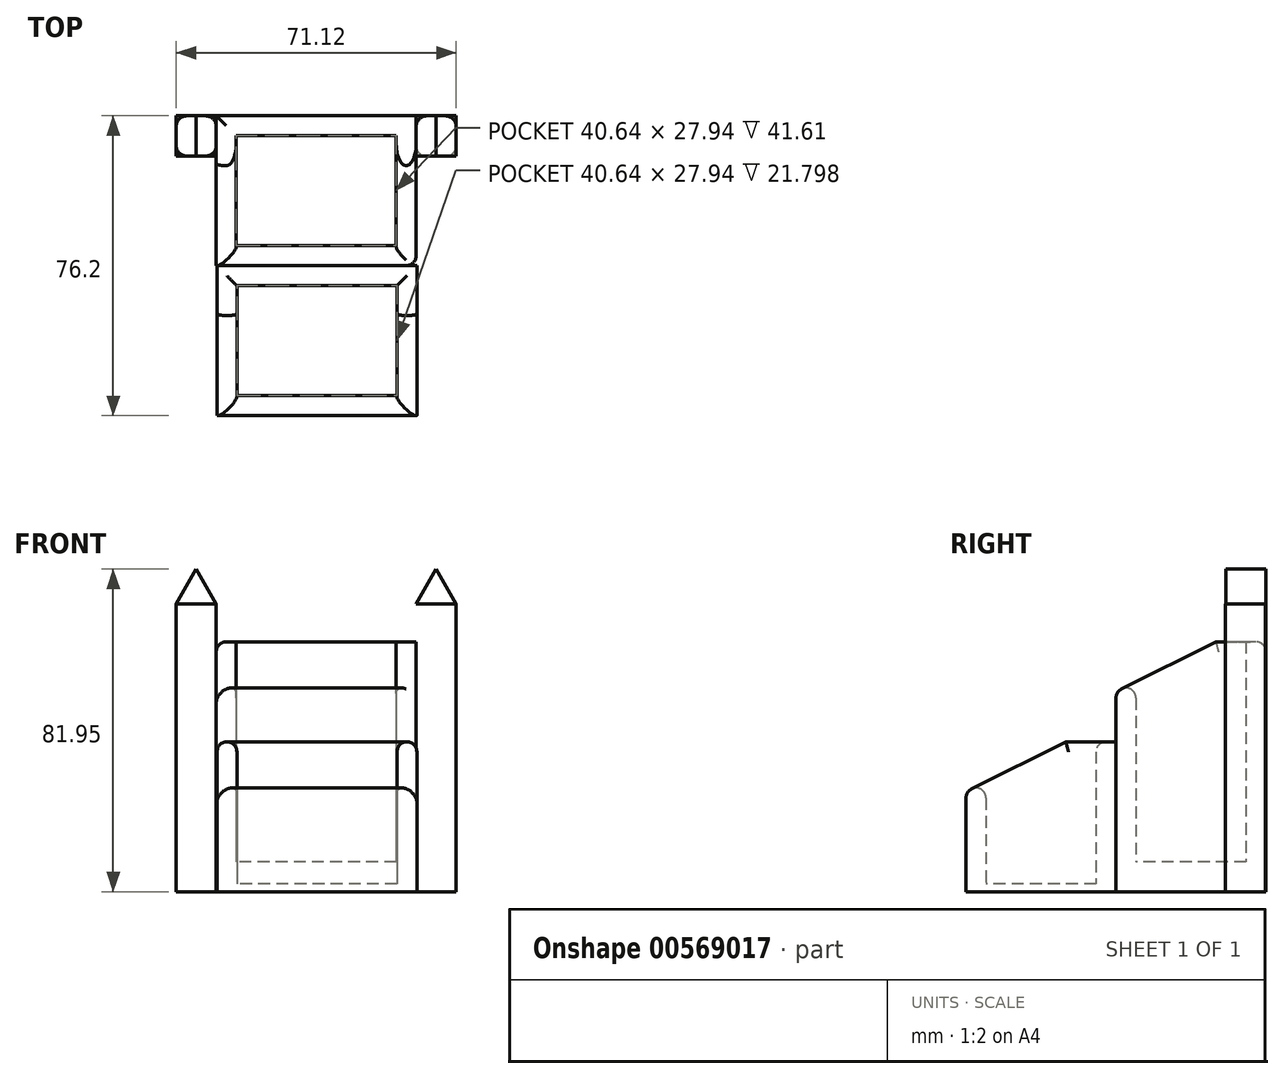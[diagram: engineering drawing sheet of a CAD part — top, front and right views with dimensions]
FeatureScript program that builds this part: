
annotation { "Feature Type Name" : "Feature", "Feature Type Description" : "" }
export const myFeature = defineFeature(function(context is Context, id is Id, definition is map)
    precondition{}
    {
        {
            var Q0;
            Q0=qCreatedBy(makeId("Top.planeOp"),FACE);
            var sketch = newSketch(context, id + "F0", { "sketchPlane" : qUnion([Q0])});
            skLineSegment(sketch, "E0", {"start": v(-32.91, 61.8) * mm, "end": v(-32.91, 23.7) * mm});
            skLineSegment(sketch, "E1", {"start": v(-32.91, 23.7) * mm, "end": v(17.89, 23.7) * mm});
            skLineSegment(sketch, "E2", {"start": v(17.89, 23.7) * mm, "end": v(17.89, 61.8) * mm});
            skLineSegment(sketch, "E3", {"start": v(17.89, 61.8) * mm, "end": v(-32.91, 61.8) * mm});
            skSolve(sketch);
        }
        {
            var Q0;
            Q0=qCreatedBy(makeId("Top.planeOp"),FACE);
            var sketch = newSketch(context, id + "F1", { "sketchPlane" : qUnion([Q0])});
            skLineSegment(sketch, "E4", {"start": v(-32.74, 23.7) * mm, "end": v(-32.74, -14.4) * mm});
            skLineSegment(sketch, "E5", {"start": v(-32.74, -14.4) * mm, "end": v(18.06, -14.4) * mm});
            skLineSegment(sketch, "E6", {"start": v(18.06, -14.4) * mm, "end": v(18.06, 23.7) * mm});
            skLineSegment(sketch, "E7", {"start": v(18.06, 23.7) * mm, "end": v(-32.74, 23.7) * mm});
            skSolve(sketch);
        }
        {
            var Q0;
            Q0=qCreatedBy(makeId("Top.planeOp"),FACE);
            var sketch = newSketch(context, id + "F2", { "sketchPlane" : qUnion([Q0])});
            skLineSegment(sketch, "E8", {"start": v(-27.83, 56.71) * mm, "end": v(-27.83, 28.77) * mm});
            skLineSegment(sketch, "E9", {"start": v(-27.83, 28.77) * mm, "end": v(12.8, 28.77) * mm});
            skLineSegment(sketch, "E10", {"start": v(12.8, 28.77) * mm, "end": v(12.8, 56.71) * mm});
            skLineSegment(sketch, "E11", {"start": v(12.8, 56.71) * mm, "end": v(-27.83, 56.71) * mm});
            skSolve(sketch);
        }
        {
            var Q0;
            Q0=qCreatedBy(makeId("Top.planeOp"),FACE);
            var sketch = newSketch(context, id + "F3", { "sketchPlane" : qUnion([Q0])});
            skLineSegment(sketch, "E12", {"start": v(-27.66, 18.61) * mm, "end": v(-27.66, -9.33) * mm});
            skLineSegment(sketch, "E13", {"start": v(-27.66, -9.33) * mm, "end": v(12.98, -9.33) * mm});
            skLineSegment(sketch, "E14", {"start": v(12.98, -9.33) * mm, "end": v(12.98, 18.61) * mm});
            skLineSegment(sketch, "E15", {"start": v(12.98, 18.61) * mm, "end": v(-27.66, 18.61) * mm});
            skSolve(sketch);
        }
        {
            var Q0;
            Q0 = qSketchRegion(id + "F0", true);
            extrude(context, id + "F4", {"entities" : qUnion([Q0]), "depth" : 63.5 * mm, "offsetDistance" : 25.4 * mm});
        }
        {
            var Q0;
            Q0 = qSketchRegion(id + "F1", true);
            extrude(context, id + "F5", {"entities" : qUnion([Q0]), "depth" : 38.1 * mm, "offsetDistance" : 25.4 * mm});
        }
        {
            var Q0;
            Q0 = qSketchRegion(id + "F2", true);
            extrude(context, id + "F6", {"entities" : qUnion([Q0]), "operationType" : NewBodyOperationType.REMOVE, "depth" : 63.5 * mm, "offsetDistance" : 25.4 * mm, "hasSecondDirection" : true, "secondDirectionOppositeDirection" : false, "secondDirectionDepth" : 7.62 * mm});
        }
        {
            var Q0;
            Q0 = qSketchRegion(id + "F3", true);
            extrude(context, id + "F7", {"entities" : qUnion([Q0]), "operationType" : NewBodyOperationType.REMOVE, "depth" : 61.2 * mm, "offsetDistance" : 25.4 * mm, "hasSecondDirection" : true, "secondDirectionOppositeDirection" : false, "secondDirectionDepth" : 2.03 * mm});
        }
        {
            var Q0;
            Q0=qCreatedBy(makeId("Top.planeOp"),FACE);
            var sketch = newSketch(context, id + "F8", { "sketchPlane" : qUnion([Q0])});
            skLineSegment(sketch, "E16", {"start": v(-32.91, 61.73) * mm, "end": v(-43.07, 61.73) * mm});
            skLineSegment(sketch, "E17", {"start": v(-43.07, 61.73) * mm, "end": v(-43.07, 51.57) * mm});
            skLineSegment(sketch, "E18", {"start": v(-43.07, 51.57) * mm, "end": v(-32.91, 51.57) * mm});
            skLineSegment(sketch, "E19", {"start": v(-32.91, 51.57) * mm, "end": v(-32.91, 61.73) * mm});
            skLineSegment(sketch, "E20", {"start": v(17.89, 61.7) * mm, "end": v(17.89, 51.54) * mm});
            skLineSegment(sketch, "E21", {"start": v(17.89, 51.54) * mm, "end": v(28.05, 51.54) * mm});
            skLineSegment(sketch, "E22", {"start": v(28.05, 51.54) * mm, "end": v(28.05, 61.7) * mm});
            skLineSegment(sketch, "E23", {"start": v(28.05, 61.7) * mm, "end": v(17.89, 61.7) * mm});
            skSolve(sketch);
        }
        {
            var Q0;
            Q0 = qSketchRegion(id + "F8", true);
            extrude(context, id + "F9", {"entities" : qUnion([Q0]), "depth" : 73.15 * mm, "offsetDistance" : 25.4 * mm});
        }
        {
            var Q0;
            Q0=qCreatedBy(makeId("Front.planeOp"),FACE);
            var sketch = newSketch(context, id + "F10", { "sketchPlane" : qUnion([Q0])});
            skLineSegment(sketch, "E24", {"start": v(-43.07, 73.15) * mm, "end": v(-32.91, 73.15) * mm});
            skLineSegment(sketch, "E25", {"start": v(-32.91, 73.15) * mm, "end": v(-38, 81.95) * mm});
            skLineSegment(sketch, "E26", {"start": v(-38, 81.95) * mm, "end": v(-43.07, 73.15) * mm});
            skLineSegment(sketch, "E27", {"start": v(17.89, 73.15) * mm, "end": v(28.05, 73.15) * mm});
            skLineSegment(sketch, "E28", {"start": v(28.05, 73.15) * mm, "end": v(22.97, 81.95) * mm});
            skLineSegment(sketch, "E29", {"start": v(22.97, 81.95) * mm, "end": v(17.89, 73.15) * mm});
            skSolve(sketch);
        }
        {
            var Q0;
            Q0 = qSketchRegion(id + "F10", true);
            extrude(context, id + "F11", {"entities" : qUnion([Q0]), "oppositeDirection" : true, "depth" : 61.77 * mm, "offsetDistance" : 25.4 * mm, "hasSecondDirection" : true, "secondDirectionOppositeDirection" : true, "secondDirectionDepth" : 51.56 * mm});
        }
        {
            var Q0;
            Q0=makeQuery(id+"F5.opExtrude","CAP_EDGE",EDGE,{"disambiguationData":[OSD([sQuery(id+"F1.wireOp",EDGE,"E5")])],"isStart":false});
            var Q1;
            Q1=makeQuery(id+"F4.opExtrude","CAP_EDGE",EDGE,{"disambiguationData":[OSD([sQuery(id+"F0.wireOp",EDGE,"E1")])],"isStart":false});
            chamfer(context, id + "F12", {"entities" : qUnion([Q0, Q1]), "chamferType" : ChamferType.TWO_OFFSETS, "width1" : 25.4 * mm, "oppositeDirection" : false, "width2" : 12.7 * mm, "tangentPropagation" : true});
        }
        {
            var Q0;
            Q0=makeQuery(id+"F7.boolean.opBoolean","INTERSECT",EDGE,{"derivedFrom":[makeQuery(id+"F5.opExtrude","CAP_FACE",FACE,{"disambiguationData":[OSD([sQuery(id+"F1.wireOp",EDGE,"E4"),sQuery(id+"F1.wireOp",EDGE,"E5"),sQuery(id+"F1.wireOp",EDGE,"E6"),sQuery(id+"F1.wireOp",EDGE,"E7")])],"isStart":false}),makeQuery(id+"F7.opExtrude","SWEPT_FACE",FACE,{"disambiguationData":[OSD([sQuery(id+"F3.wireOp",EDGE,"E15")])]})]});
            var Q1;
            Q1=makeQuery(id+"F7.boolean.opBoolean","INTERSECT",EDGE,{"derivedFrom":[makeQuery(id+"F5.opExtrude","CAP_FACE",FACE,{"disambiguationData":[OSD([sQuery(id+"F1.wireOp",EDGE,"E4"),sQuery(id+"F1.wireOp",EDGE,"E5"),sQuery(id+"F1.wireOp",EDGE,"E6"),sQuery(id+"F1.wireOp",EDGE,"E7")])],"isStart":false}),makeQuery(id+"F7.opExtrude","SWEPT_FACE",FACE,{"disambiguationData":[OSD([sQuery(id+"F3.wireOp",EDGE,"E12")])]})]});
            var Q2;
            Q2=makeQuery(id+"F12.opChamfer","BLEND_EDGE",EDGE,{"blendedFrom":[makeQuery(id+"F5.opExtrude","CAP_EDGE",EDGE,{"disambiguationData":[OSD([sQuery(id+"F1.wireOp",EDGE,"E5")])],"isStart":false}),makeQuery(id+"F7.boolean.opBoolean","COPY",FACE,{"derivedFrom":makeQuery(id+"F7.opExtrude","SWEPT_FACE",FACE,{"disambiguationData":[OSD([sQuery(id+"F3.wireOp",EDGE,"E12")])]})})],"blendedInto":[makeQuery(id+"F7.boolean.opBoolean","COPY",FACE,{"derivedFrom":makeQuery(id+"F7.opExtrude","SWEPT_FACE",FACE,{"disambiguationData":[OSD([sQuery(id+"F3.wireOp",EDGE,"E12")])]})})]});
            var Q3;
            Q3=makeQuery(id+"F12.opChamfer","BLEND_EDGE",EDGE,{"blendedFrom":[makeQuery(id+"F5.opExtrude","CAP_EDGE",EDGE,{"disambiguationData":[OSD([sQuery(id+"F1.wireOp",EDGE,"E5")])],"isStart":false}),makeQuery(id+"F7.boolean.opBoolean","COPY",FACE,{"derivedFrom":makeQuery(id+"F7.opExtrude","SWEPT_FACE",FACE,{"disambiguationData":[OSD([sQuery(id+"F3.wireOp",EDGE,"E14")])]})})],"blendedInto":[makeQuery(id+"F7.boolean.opBoolean","COPY",FACE,{"derivedFrom":makeQuery(id+"F7.opExtrude","SWEPT_FACE",FACE,{"disambiguationData":[OSD([sQuery(id+"F3.wireOp",EDGE,"E14")])]})})]});
            var Q4;
            Q4=makeQuery(id+"F7.boolean.opBoolean","INTERSECT",EDGE,{"derivedFrom":[makeQuery(id+"F5.opExtrude","CAP_FACE",FACE,{"disambiguationData":[OSD([sQuery(id+"F1.wireOp",EDGE,"E4"),sQuery(id+"F1.wireOp",EDGE,"E5"),sQuery(id+"F1.wireOp",EDGE,"E6"),sQuery(id+"F1.wireOp",EDGE,"E7")])],"isStart":false}),makeQuery(id+"F7.opExtrude","SWEPT_FACE",FACE,{"disambiguationData":[OSD([sQuery(id+"F3.wireOp",EDGE,"E14")])]})]});
            var Q5;
            Q5=makeQuery(id+"F12.opChamfer","BLEND_EDGE",EDGE,{"blendedFrom":[makeQuery(id+"F5.opExtrude","CAP_EDGE",EDGE,{"disambiguationData":[OSD([sQuery(id+"F1.wireOp",EDGE,"E5")])],"isStart":false}),makeQuery(id+"F7.boolean.opBoolean","COPY",FACE,{"derivedFrom":makeQuery(id+"F7.opExtrude","SWEPT_FACE",FACE,{"disambiguationData":[OSD([sQuery(id+"F3.wireOp",EDGE,"E13")])]})})],"blendedInto":[makeQuery(id+"F7.boolean.opBoolean","COPY",FACE,{"derivedFrom":makeQuery(id+"F7.opExtrude","SWEPT_FACE",FACE,{"disambiguationData":[OSD([sQuery(id+"F3.wireOp",EDGE,"E13")])]})})]});
            var Q6;
            Q6=makeQuery(id+"F12.opChamfer","BLEND_EDGE",EDGE,{"blendedFrom":[makeQuery(id+"F4.opExtrude","CAP_EDGE",EDGE,{"disambiguationData":[OSD([sQuery(id+"F0.wireOp",EDGE,"E1")])],"isStart":false}),makeQuery(id+"F6.boolean.opBoolean","COPY",FACE,{"derivedFrom":makeQuery(id+"F6.opExtrude","SWEPT_FACE",FACE,{"disambiguationData":[OSD([sQuery(id+"F2.wireOp",EDGE,"E9")])]})})],"blendedInto":[makeQuery(id+"F6.boolean.opBoolean","COPY",FACE,{"derivedFrom":makeQuery(id+"F6.opExtrude","SWEPT_FACE",FACE,{"disambiguationData":[OSD([sQuery(id+"F2.wireOp",EDGE,"E9")])]})})]});
            var Q7;
            Q7=makeQuery(id+"F12.opChamfer","BLEND_EDGE",EDGE,{"blendedFrom":[makeQuery(id+"F4.opExtrude","CAP_EDGE",EDGE,{"disambiguationData":[OSD([sQuery(id+"F0.wireOp",EDGE,"E1")])],"isStart":false}),makeQuery(id+"F6.boolean.opBoolean","COPY",FACE,{"derivedFrom":makeQuery(id+"F6.opExtrude","SWEPT_FACE",FACE,{"disambiguationData":[OSD([sQuery(id+"F2.wireOp",EDGE,"E8")])]})})],"blendedInto":[makeQuery(id+"F6.boolean.opBoolean","COPY",FACE,{"derivedFrom":makeQuery(id+"F6.opExtrude","SWEPT_FACE",FACE,{"disambiguationData":[OSD([sQuery(id+"F2.wireOp",EDGE,"E8")])]})})]});
            var Q8;
            Q8=makeQuery(id+"F6.boolean.opBoolean","COPY",EDGE,{"derivedFrom":makeQuery(id+"F6.opExtrude","CAP_EDGE",EDGE,{"disambiguationData":[OSD([sQuery(id+"F2.wireOp",EDGE,"E8")])],"isStart":false})});
            var Q9;
            Q9=makeQuery(id+"F6.boolean.opBoolean","COPY",EDGE,{"derivedFrom":makeQuery(id+"F6.opExtrude","CAP_EDGE",EDGE,{"disambiguationData":[OSD([sQuery(id+"F2.wireOp",EDGE,"E11")])],"isStart":false})});
            var Q10;
            Q10=makeQuery(id+"F6.boolean.opBoolean","COPY",EDGE,{"derivedFrom":makeQuery(id+"F6.opExtrude","CAP_EDGE",EDGE,{"disambiguationData":[OSD([sQuery(id+"F2.wireOp",EDGE,"E10")])],"isStart":false})});
            var Q11;
            Q11=makeQuery(id+"F12.opChamfer","BLEND_EDGE",EDGE,{"blendedFrom":[makeQuery(id+"F4.opExtrude","CAP_EDGE",EDGE,{"disambiguationData":[OSD([sQuery(id+"F0.wireOp",EDGE,"E1")])],"isStart":false}),makeQuery(id+"F6.boolean.opBoolean","COPY",FACE,{"derivedFrom":makeQuery(id+"F6.opExtrude","SWEPT_FACE",FACE,{"disambiguationData":[OSD([sQuery(id+"F2.wireOp",EDGE,"E10")])]})})],"blendedInto":[makeQuery(id+"F6.boolean.opBoolean","COPY",FACE,{"derivedFrom":makeQuery(id+"F6.opExtrude","SWEPT_FACE",FACE,{"disambiguationData":[OSD([sQuery(id+"F2.wireOp",EDGE,"E10")])]})})]});
            var Q12;
            Q12=makeQuery(id+"F12.opChamfer","BLEND_EDGE",EDGE,{"blendedFrom":[makeQuery(id+"F4.opExtrude","CAP_EDGE",EDGE,{"disambiguationData":[OSD([sQuery(id+"F0.wireOp",EDGE,"E1")])],"isStart":false}),makeQuery(id+"F4.opExtrude","SWEPT_FACE",FACE,{"disambiguationData":[OSD([sQuery(id+"F0.wireOp",EDGE,"E0")])]})],"blendedInto":[makeQuery(id+"F4.opExtrude","SWEPT_FACE",FACE,{"disambiguationData":[OSD([sQuery(id+"F0.wireOp",EDGE,"E0")])]})]});
            var Q13;
            Q13=makeQuery(id+"F4.opExtrude","CAP_EDGE",EDGE,{"disambiguationData":[OSD([sQuery(id+"F0.wireOp",EDGE,"E3")])],"isStart":false});
            var Q14;
            Q14=makeQuery(id+"F12.opChamfer","BLEND_EDGE",EDGE,{"blendedFrom":[makeQuery(id+"F4.opExtrude","CAP_EDGE",EDGE,{"disambiguationData":[OSD([sQuery(id+"F0.wireOp",EDGE,"E1")])],"isStart":false}),makeQuery(id+"F4.opExtrude","SWEPT_FACE",FACE,{"disambiguationData":[OSD([sQuery(id+"F0.wireOp",EDGE,"E2")])]})],"blendedInto":[makeQuery(id+"F4.opExtrude","SWEPT_FACE",FACE,{"disambiguationData":[OSD([sQuery(id+"F0.wireOp",EDGE,"E2")])]})]});
            var Q15;
            Q15=makeQuery(id+"F5.opExtrude","CAP_EDGE",EDGE,{"disambiguationData":[OSD([sQuery(id+"F1.wireOp",EDGE,"E6")])],"isStart":false});
            var Q16;
            Q16=makeQuery(id+"F12.opChamfer","BLEND_EDGE",EDGE,{"blendedFrom":[makeQuery(id+"F5.opExtrude","CAP_EDGE",EDGE,{"disambiguationData":[OSD([sQuery(id+"F1.wireOp",EDGE,"E5")])],"isStart":false}),makeQuery(id+"F5.opExtrude","SWEPT_FACE",FACE,{"disambiguationData":[OSD([sQuery(id+"F1.wireOp",EDGE,"E6")])]})],"blendedInto":[makeQuery(id+"F5.opExtrude","SWEPT_FACE",FACE,{"disambiguationData":[OSD([sQuery(id+"F1.wireOp",EDGE,"E6")])]})]});
            var Q17;
            {var subQ0=sQuery(id+"F1.wireOp",EDGE,"E5");Q17=makeQuery(id+"F12.opChamfer","BLEND_EDGE",EDGE,{"blendedFrom":[makeQuery(id+"F5.opExtrude","CAP_EDGE",EDGE,{"disambiguationData":[OSD([subQ0])],"isStart":false}),makeQuery(id+"F5.opExtrude","SWEPT_FACE",FACE,{"disambiguationData":[OSD([subQ0])]})],"blendedInto":[makeQuery(id+"F5.opExtrude","SWEPT_FACE",FACE,{"disambiguationData":[OSD([subQ0])]})]});}
            var Q18;
            Q18=makeQuery(id+"F12.opChamfer","BLEND_EDGE",EDGE,{"blendedFrom":[makeQuery(id+"F5.opExtrude","CAP_EDGE",EDGE,{"disambiguationData":[OSD([sQuery(id+"F1.wireOp",EDGE,"E5")])],"isStart":false}),makeQuery(id+"F5.opExtrude","SWEPT_FACE",FACE,{"disambiguationData":[OSD([sQuery(id+"F1.wireOp",EDGE,"E4")])]})],"blendedInto":[makeQuery(id+"F5.opExtrude","SWEPT_FACE",FACE,{"disambiguationData":[OSD([sQuery(id+"F1.wireOp",EDGE,"E4")])]})]});
            var Q19;
            Q19=makeQuery(id+"F5.opExtrude","CAP_EDGE",EDGE,{"disambiguationData":[OSD([sQuery(id+"F1.wireOp",EDGE,"E4")])],"isStart":false});
            var Q20;
            {var subQ0=sQuery(id+"F0.wireOp",EDGE,"E1");Q20=makeQuery(id+"F12.opChamfer","BLEND_EDGE",EDGE,{"blendedFrom":[makeQuery(id+"F4.opExtrude","CAP_EDGE",EDGE,{"disambiguationData":[OSD([subQ0])],"isStart":false}),makeQuery(id+"F4.opExtrude","SWEPT_FACE",FACE,{"disambiguationData":[OSD([subQ0])]})],"blendedInto":[makeQuery(id+"F4.opExtrude","SWEPT_FACE",FACE,{"disambiguationData":[OSD([subQ0])]})]});}
            var Q21;
            Q21=makeQuery(id+"F4.opExtrude","CAP_EDGE",EDGE,{"disambiguationData":[OSD([sQuery(id+"F0.wireOp",EDGE,"E0")])],"isStart":false});
            var Q22;
            Q22=makeQuery(id+"F9.opExtrude","SWEPT_EDGE",EDGE,{"disambiguationData":[OSD([sQuery(id+"F8.wireOp",EDGE,"E17"),sQuery(id+"F8.wireOp",EDGE,"E18")])]});
            var Q23;
            Q23=makeQuery(id+"F9.opExtrude","SWEPT_EDGE",EDGE,{"disambiguationData":[OSD([sQuery(id+"F8.wireOp",EDGE,"E16"),sQuery(id+"F8.wireOp",EDGE,"E17")])]});
            var Q24;
            Q24=makeQuery(id+"F9.opExtrude","SWEPT_EDGE",EDGE,{"disambiguationData":[OSD([sQuery(id+"F8.wireOp",EDGE,"E22"),sQuery(id+"F8.wireOp",EDGE,"E23")])]});
            var Q25;
            Q25=makeQuery(id+"F4.opExtrude","SWEPT_EDGE",EDGE,{"disambiguationData":[OSD([sQuery(id+"F0.wireOp",EDGE,"E1"),sQuery(id+"F0.wireOp",EDGE,"E2")])]});
            var Q26;
            Q26=makeQuery(id+"F9.opExtrude","SWEPT_EDGE",EDGE,{"disambiguationData":[OSD([sQuery(id+"F8.wireOp",EDGE,"E16"),sQuery(id+"F8.wireOp",EDGE,"E19")])]});
            var Q27;
            Q27=makeQuery(id+"F9.opExtrude","SWEPT_EDGE",EDGE,{"disambiguationData":[OSD([sQuery(id+"F8.wireOp",EDGE,"E20"),sQuery(id+"F8.wireOp",EDGE,"E21")])]});
            var Q28;
            Q28=makeQuery(id+"F9.opExtrude","SWEPT_EDGE",EDGE,{"disambiguationData":[OSD([sQuery(id+"F8.wireOp",EDGE,"E21"),sQuery(id+"F8.wireOp",EDGE,"E22")])]});
            var Q29;
            Q29=makeQuery(id+"F9.opExtrude","SWEPT_EDGE",EDGE,{"disambiguationData":[OSD([sQuery(id+"F8.wireOp",EDGE,"E18"),sQuery(id+"F8.wireOp",EDGE,"E19")])]});
            var Q30;
            Q30=makeQuery(id+"F9.opExtrude","SWEPT_EDGE",EDGE,{"disambiguationData":[OSD([sQuery(id+"F8.wireOp",EDGE,"E20"),sQuery(id+"F8.wireOp",EDGE,"E23")])]});
            fillet(context, id + "F13", {"entities" : qUnion([Q0, Q1, Q2, Q3, Q4, Q5, Q6, Q7, Q8, Q9, Q10, Q11, Q12, Q13, Q14, Q15, Q16, Q17, Q18, Q19, Q20, Q21, Q22, Q23, Q24, Q25, Q26, Q27, Q28, Q29, Q30]), "radius" : 2.54 * mm, "tangentPropagation" : true, "allowEdgeOverflow" : false});
        }
    });
